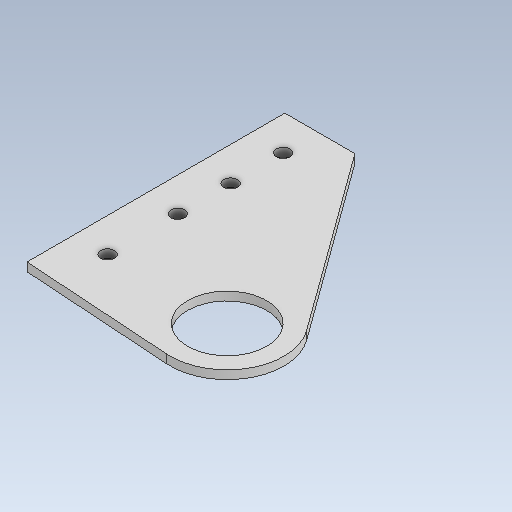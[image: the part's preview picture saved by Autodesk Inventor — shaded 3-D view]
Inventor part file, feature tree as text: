
AUTODESK INVENTOR PART (.ipt)
format: ipt  version: 2023 (Build 270158000, 158)  size: 104,448 bytes
history: native  units: in
note: dims shown in document units (in); Inventor stores cm internally (conversion verified against a paired STEP export)
features: other x3, sketch x1
ambient origin geometry x8: Origin, YZ Plane, XZ Plane, XY Plane, X Axis, Y Axis, Z Axis, Center Point
bodies: Body1 (feature_tree)
feature tree (4):
  other  "Bracket.ipt"
  other  "Solid2::Bracket.ipt"
  other  "TaggingFeature1"
  sketch  "Sketch1"  dims[d0=0.3937in]
